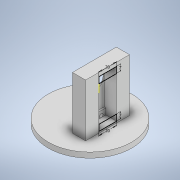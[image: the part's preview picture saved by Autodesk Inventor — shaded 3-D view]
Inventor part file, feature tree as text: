
AUTODESK INVENTOR PART (.ipt)
format: ipt  version: 2022 (Build 260153000, 153)  size: 224,768 bytes
history: native  units: in
note: dims shown in document units (in); Inventor stores cm internally (conversion verified against a paired STEP export)
features: sketch x10, extrude x9
ambient origin geometry x8: Origin, YZ Plane, XZ Plane, XY Plane, X Axis, Y Axis, Z Axis, Center Point
bodies: Solid1 (feature_tree)
feature tree (19):
  extrude  "Extrusion1"  Depth=0.2362in TaperAngle=0.0deg
  extrude  "Extrusion2"  Depth=0.1181in
  extrude  "Extrusion3"  Depth=0.2362in TaperAngle=0.0deg
  extrude  "Extrusion4"  Depth=0.3937in
  extrude  "Extrusion5"  Depth=0.5906in
  extrude  "Extrusion6"  Depth=0.9843in
  extrude  "Extrusion7"  Depth=0.0787in
  sketch  "Sketch8"  dims[d17=1.5748in d18=0.7874in]
  extrude  "Extrusion8"  Depth=0.7874in
  extrude  "Extrusion9"  Depth=0.7874in
  sketch  "Sketch1"  dims[d0=3.7402in d1=0.2362in d2=0.0in]
  sketch  "Sketch2"  dims[d3=0.5512in d4=0.1181in]
  sketch  "Sketch3"  dims[d5=0.1181in d6=0.2362in d7=0.0in]
  sketch  "Sketch4"  dims[d8=0.1969in d9=0.3937in]
  sketch  "Sketch5"  dims[d10=0.3937in d11=0.5906in]
  sketch  "Sketch6"  dims[d12=0.9843in d13=0.9843in]
  sketch  "Sketch7"  dims[d14=2.3622in d15=0.0in d16=0.0787in]
  sketch  "Sketch9"  dims[d19=0.7874in d20=0.0in d21=0.1969in]
  sketch  "Sketch10"  dims[d22=1.4173in d23=0.1969in d24=1.4173in d25=0.1575in d26=0.1575in d27=0.7874in d28=0.0in d29=0.1969in d30=0.5512in d31=0.1969in d32=0.5512in d33=0.1575in d34=0.1575in d35=0.7874in d36=0.0in d37=0.3937in d38=1.9685in d39=0.1969in d40=0.3937in d41=0.3937in d42=0.3937in d43=1.2205in d44=1.5748in d45=0.5512in d46=0.0in d47=0.7874in d48=0.2756in d49=0.7874in d50=0.2756in d51=0.2756in d52=0.4724in d53=0.0in d54=0.0787in d55=0.0in d56=0.0in d57=0.0in d58=0.0in d59=0.0in]
